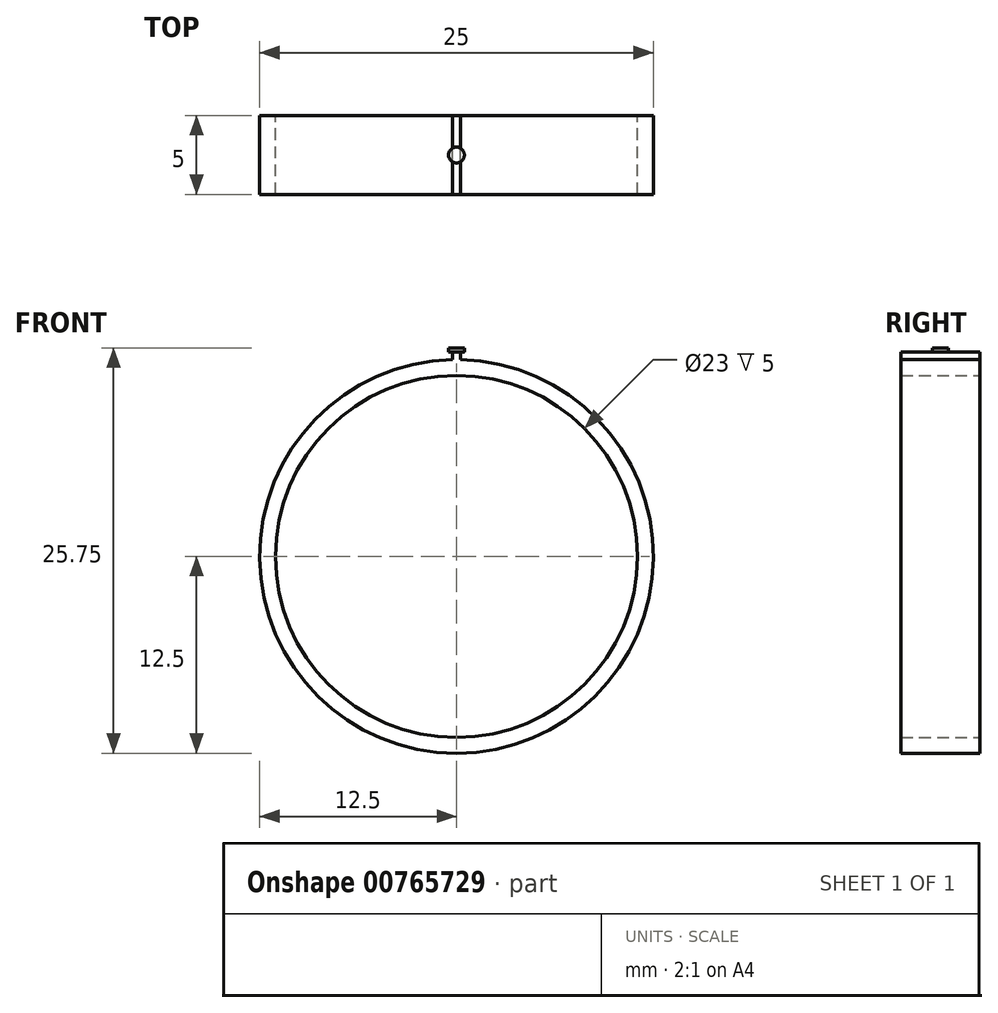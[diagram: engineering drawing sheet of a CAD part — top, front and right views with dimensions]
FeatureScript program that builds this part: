
annotation { "Feature Type Name" : "Feature", "Feature Type Description" : "" }
export const myFeature = defineFeature(function(context is Context, id is Id, definition is map)
    precondition{}
    {
        {
            var Q0;
            Q0=qCreatedBy(makeId("Front.planeOp"),FACE);
            var sketch = newSketch(context, id + "F0", { "sketchPlane" : qUnion([Q0])});
            skCircle(sketch, "E0", {"center": v(0, 0) * mm, "radius": 11.5 * mm});
            skCircle(sketch, "E1", {"center": v(0, 0) * mm, "radius": 12.5 * mm});
            skSolve(sketch);
        }
        {
            var Q0;
            Q0 = qSketchRegion(id + "F0", true);
            extrude(context, id + "F1", {"entities" : qUnion([Q0]), "endBound" : BoundingType.SYMMETRIC, "depth" : 5 * mm, "offsetDistance" : 25 * mm});
        }
        {
            var Q0;
            Q0=qCreatedBy(makeId("Front.planeOp"),FACE);
            var sketch = newSketch(context, id + "F2", { "sketchPlane" : qUnion([Q0])});
            skLineSegment(sketch, "E2", {"start": v(0, 0) * mm, "end": v(0, 13) * mm});
            skLineSegment(sketch, "E3", {"start": v(-0.25, 13) * mm, "end": v(0, 13) * mm});
            skLineSegment(sketch, "E4", {"start": v(0, 13) * mm, "end": v(0.25, 13) * mm});
            skLineSegment(sketch, "E5", {"start": v(-0.25, 13) * mm, "end": v(-0.25, 12) * mm});
            skLineSegment(sketch, "E6", {"start": v(-0.25, 12) * mm, "end": v(0.25, 12) * mm});
            skLineSegment(sketch, "E7", {"start": v(0.25, 12) * mm, "end": v(0.25, 13) * mm});
            skSolve(sketch);
        }
        {
            var Q0;
            Q0 = qSketchRegion(id + "F2", true);
            extrude(context, id + "F3", {"entities" : qUnion([Q0]), "operationType" : NewBodyOperationType.ADD, "endBound" : BoundingType.SYMMETRIC, "depth" : 5 * mm, "offsetDistance" : 25 * mm});
        }
        {
            var Q0;
            Q0=qCreatedBy(makeId("Top.planeOp"),FACE);
            var sketch = newSketch(context, id + "F4", { "sketchPlane" : qUnion([Q0])});
            skLineSegment(sketch, "E8", {"start": v(0, 0) * mm, "end": v(0, 37.1) * mm, "construction": true});
            skSolve(sketch);
        }
        {
            var Q0;
            Q0=qCreatedBy(makeId("Front.planeOp"),FACE);
            var sketch = newSketch(context, id + "F5", { "sketchPlane" : qUnion([Q0])});
            skLineSegment(sketch, "E9", {"start": v(0, 0) * mm, "end": v(0, 13.25) * mm});
            skLineSegment(sketch, "E10", {"start": v(0, 13.25) * mm, "end": v(-0.5, 13.25) * mm});
            skLineSegment(sketch, "E11", {"start": v(0, 13.25) * mm, "end": v(0.5, 13.25) * mm});
            skLineSegment(sketch, "E12", {"start": v(-0.5, 13.25) * mm, "end": v(-0.5, 13) * mm});
            skLineSegment(sketch, "E13", {"start": v(-0.5, 13) * mm, "end": v(0.5, 13) * mm});
            skLineSegment(sketch, "E14", {"start": v(0.5, 13) * mm, "end": v(0.5, 13.25) * mm});
            skSolve(sketch);
        }
        {
            var Q0;
            Q0 = qSketchRegion(id + "F5", true);
            extrude(context, id + "F6", {"entities" : qUnion([Q0]), "endBound" : BoundingType.SYMMETRIC, "depth" : 1 * mm, "offsetDistance" : 25 * mm});
        }
        {
            var Q0;
            Q0=makeQuery(id+"F6.opExtrude","CAP_EDGE",EDGE,{"disambiguationData":[OSD([sQuery(id+"F5.wireOp",EDGE,"E14")])],"isStart":true});
            var Q1;
            Q1=makeQuery(id+"F6.opExtrude","CAP_EDGE",EDGE,{"disambiguationData":[OSD([sQuery(id+"F5.wireOp",EDGE,"E12")])],"isStart":true});
            var Q2;
            Q2=makeQuery(id+"F6.opExtrude","CAP_EDGE",EDGE,{"disambiguationData":[OSD([sQuery(id+"F5.wireOp",EDGE,"E12")])],"isStart":false});
            var Q3;
            Q3=makeQuery(id+"F6.opExtrude","CAP_EDGE",EDGE,{"disambiguationData":[OSD([sQuery(id+"F5.wireOp",EDGE,"E14")])],"isStart":false});
            fillet(context, id + "F7", {"entities" : qUnion([Q0, Q1, Q2, Q3]), "radius" : 0.5 * mm, "tangentPropagation" : true, "allowEdgeOverflow" : false});
        }
    });
